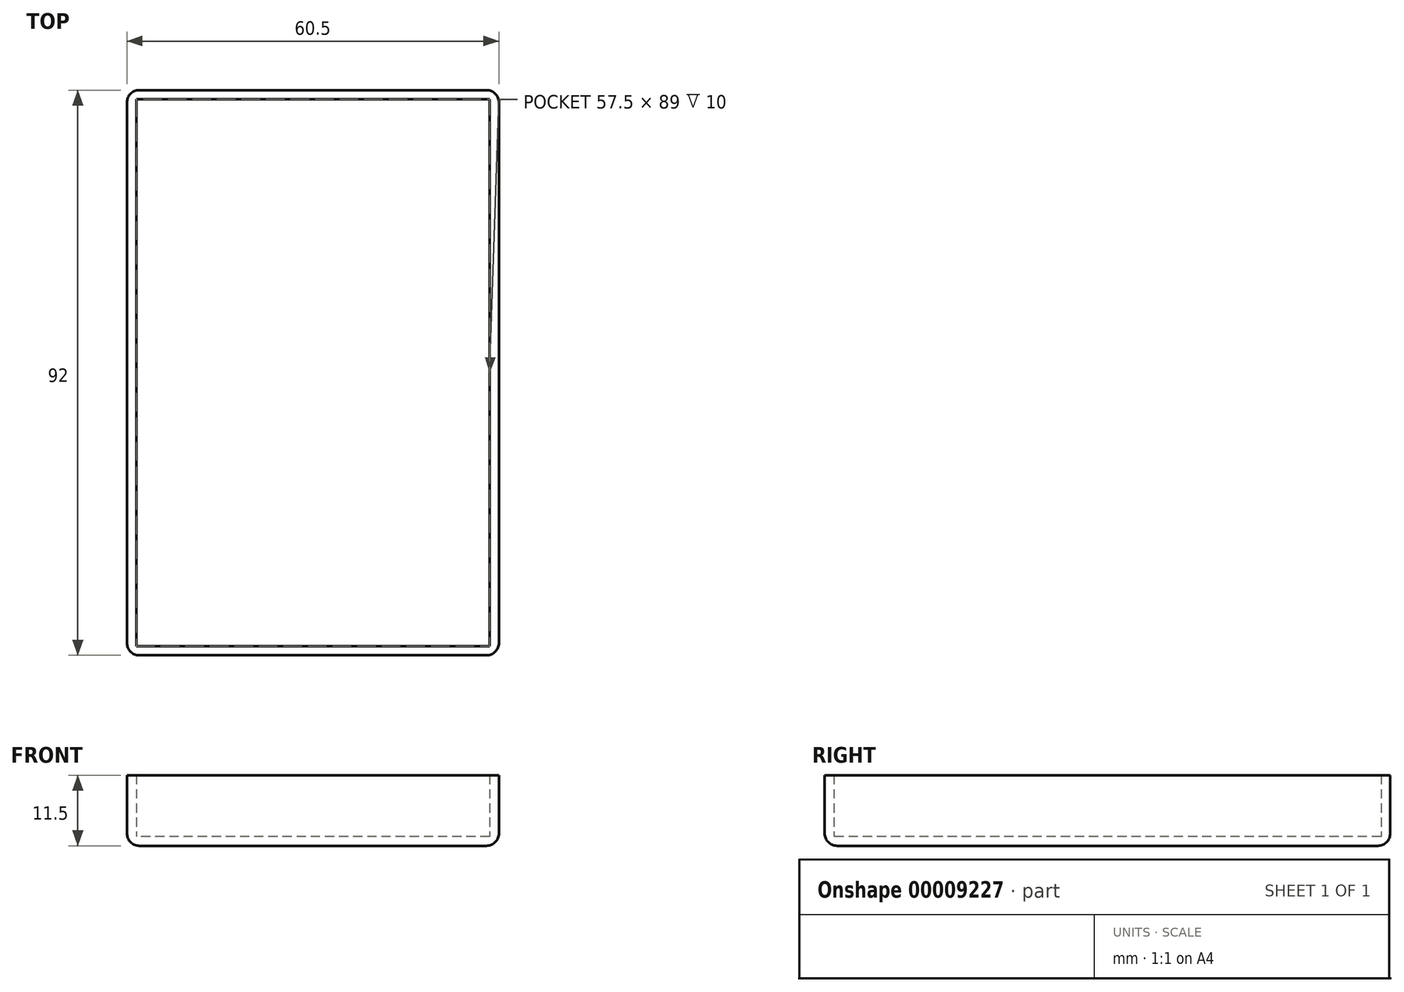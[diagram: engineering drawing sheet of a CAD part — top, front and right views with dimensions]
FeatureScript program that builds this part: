
annotation { "Feature Type Name" : "Feature", "Feature Type Description" : "" }
export const myFeature = defineFeature(function(context is Context, id is Id, definition is map)
    precondition{}
    {
        {
            var Q0;
            Q0=qCreatedBy(makeId("Top.planeOp"),FACE);
            var sketch = newSketch(context, id + "F0", { "sketchPlane" : qUnion([Q0])});
            skLineSegment(sketch, "E0.rect.bottom", {"start": v(30.25, 46) * mm, "end": v(-30.25, 46) * mm});
            skLineSegment(sketch, "E0.rect.top", {"start": v(30.25, -46) * mm, "end": v(-30.25, -46) * mm});
            skLineSegment(sketch, "E0.rect.left", {"start": v(30.25, 46) * mm, "end": v(30.25, -46) * mm});
            skLineSegment(sketch, "E0.rect.right", {"start": v(-30.25, 46) * mm, "end": v(-30.25, -46) * mm});
            skPoint(sketch, "E0.rect.middle", {"position": v(0, 0) * mm});
            skSolve(sketch);
        }
        {
            var Q0;
            Q0=makeQuery(id+"F0.imprint","IMPRINT",FACE,{"disambiguationData":[TD([[makeQuery(id+"F0.imprint","IMPRINT",EDGE,{"derivedFrom":sQuery(id+"F0.wireOp",EDGE,"E0.rect.bottom")}),1.0]])]});
            extrude(context, id + "F1", {"entities" : qUnion([Q0]), "depth" : 11.5 * mm});
        }
        {
            var Q0;
            Q0=makeQuery(id+"F1.opExtrude","CAP_FACE",FACE,{"disambiguationData":[OSD([sQuery(id+"F0.wireOp",EDGE,"E0.rect.bottom"),sQuery(id+"F0.wireOp",EDGE,"E0.rect.top"),sQuery(id+"F0.wireOp",EDGE,"E0.rect.left"),sQuery(id+"F0.wireOp",EDGE,"E0.rect.right")])],"isStart":false});
            shell(context, id + "F2", {"entities" : qUnion([Q0]), "thickness" : 1.5 * mm});
        }
        {
            var Q0;
            Q0=makeQuery(id+"F1.opExtrude","SWEPT_EDGE",EDGE,{"disambiguationData":[OSD([sQuery(id+"F0.wireOp",EDGE,"E0.rect.top"),sQuery(id+"F0.wireOp",EDGE,"E0.rect.left")])]});
            var Q1;
            Q1=makeQuery(id+"F1.opExtrude","SWEPT_EDGE",EDGE,{"disambiguationData":[OSD([sQuery(id+"F0.wireOp",EDGE,"E0.rect.top"),sQuery(id+"F0.wireOp",EDGE,"E0.rect.right")])]});
            var Q2;
            Q2=makeQuery(id+"F1.opExtrude","SWEPT_EDGE",EDGE,{"disambiguationData":[OSD([sQuery(id+"F0.wireOp",EDGE,"E0.rect.bottom"),sQuery(id+"F0.wireOp",EDGE,"E0.rect.left")])]});
            var Q3;
            Q3=makeQuery(id+"F1.opExtrude","SWEPT_EDGE",EDGE,{"disambiguationData":[OSD([sQuery(id+"F0.wireOp",EDGE,"E0.rect.bottom"),sQuery(id+"F0.wireOp",EDGE,"E0.rect.right")])]});
            var Q4;
            Q4=makeQuery(id+"F1.opExtrude","CAP_EDGE",EDGE,{"disambiguationData":[OSD([sQuery(id+"F0.wireOp",EDGE,"E0.rect.left")])],"isStart":true});
            var Q5;
            Q5=makeQuery(id+"F1.opExtrude","CAP_EDGE",EDGE,{"disambiguationData":[OSD([sQuery(id+"F0.wireOp",EDGE,"E0.rect.top")])],"isStart":true});
            var Q6;
            Q6=makeQuery(id+"F1.opExtrude","CAP_EDGE",EDGE,{"disambiguationData":[OSD([sQuery(id+"F0.wireOp",EDGE,"E0.rect.bottom")])],"isStart":true});
            var Q7;
            Q7=makeQuery(id+"F1.opExtrude","CAP_EDGE",EDGE,{"disambiguationData":[OSD([sQuery(id+"F0.wireOp",EDGE,"E0.rect.right")])],"isStart":true});
            fillet(context, id + "F3", {"entities" : qUnion([Q0, Q1, Q2, Q3, Q4, Q5, Q6, Q7]), "radius" : 2 * mm, "tangentPropagation" : true, "allowEdgeOverflow" : false});
        }
    });
